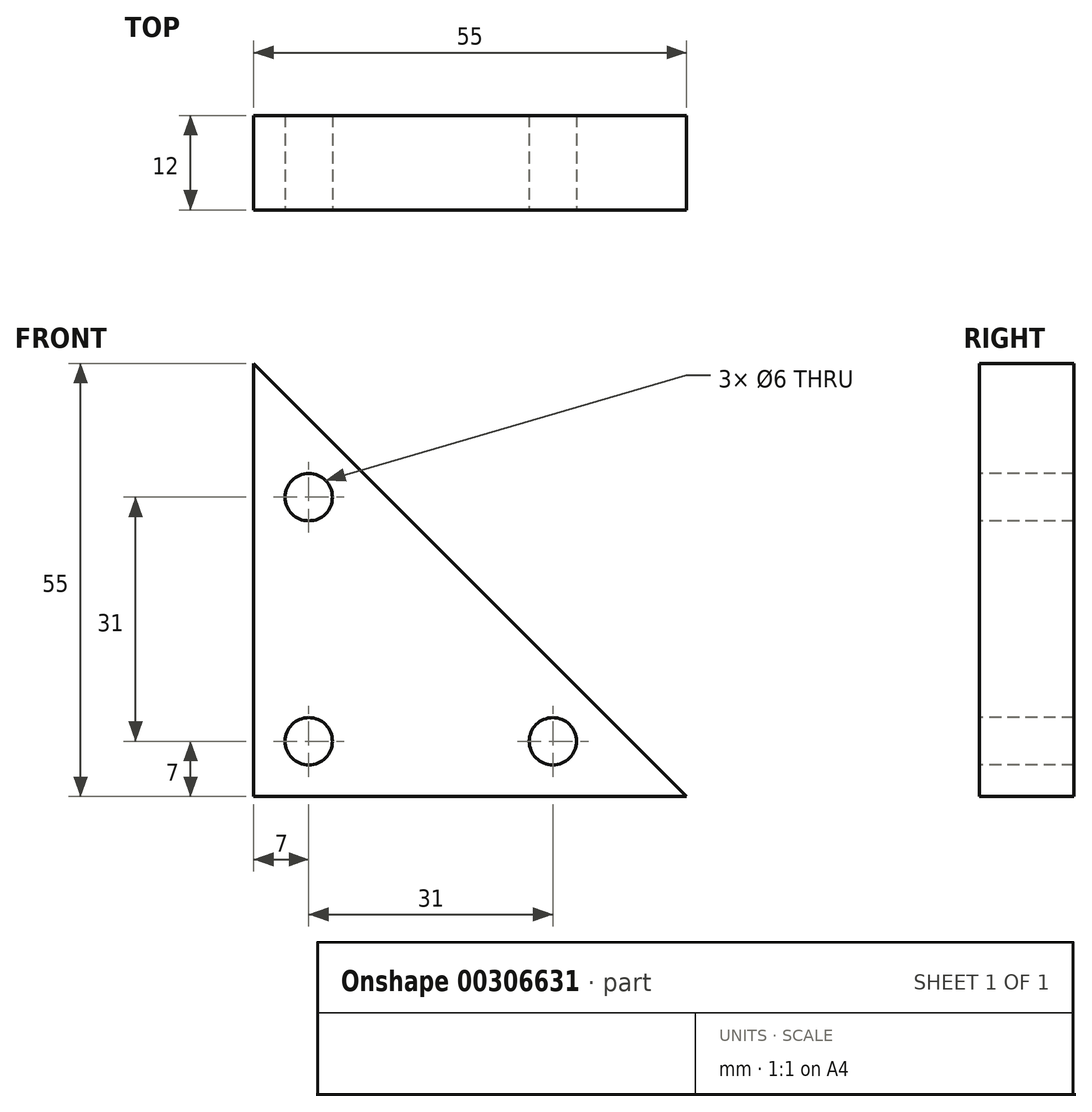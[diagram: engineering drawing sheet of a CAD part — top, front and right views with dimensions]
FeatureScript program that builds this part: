
annotation { "Feature Type Name" : "Feature", "Feature Type Description" : "" }
export const myFeature = defineFeature(function(context is Context, id is Id, definition is map)
    precondition{}
    {
        {
            var Q0;
            Q0=qCreatedBy(makeId("Front.planeOp"),FACE);
            var sketch = newSketch(context, id + "F0", { "sketchPlane" : qUnion([Q0])});
            skLineSegment(sketch, "E0", {"start": v(0, 0) * mm, "end": v(0, 55) * mm});
            skLineSegment(sketch, "E1", {"start": v(0, 55) * mm, "end": v(55, 0) * mm});
            skLineSegment(sketch, "E2", {"start": v(55, 0) * mm, "end": v(0, 0) * mm});
            skCircle(sketch, "E3", {"center": v(7, 38) * mm, "radius": 3 * mm});
            skLineSegment(sketch, "E4", {"start": v(27.5, 27.5) * mm, "end": v(0, 0) * mm, "construction": true});
            skCircle(sketch, "E5.MirrorC", {"center": v(38, 7) * mm, "radius": 3 * mm});
            skCircle(sketch, "E6", {"center": v(7, 7) * mm, "radius": 3 * mm});
            skSolve(sketch);
        }
        {
            var Q0;
            Q0=qSketchRegion(id+"F0",true);
            extrude(context, id + "F1", {"entities" : qUnion([Q0]), "oppositeDirection" : true, "depth" : 12 * mm});
        }
    });
